# Revit family: VIESSMANN - Vitocell 100-V (CVW.CVWA) 300 L
name_source: partatom
category: Wyposażenie mechaniczne
revit_build: Autodesk Revit 2017 (Build: 20160720_1515(x64)
units: mm (PartAtom-declared; Revit-internal decimal feet)

## family parameters
Numer OmniClass = 23.65.35.11.11
Oparty na płaszczyźnie roboczej = Nie
Punkt obliczania pomieszczeń = Nie
Tnij formami wycięć po wczytaniu = Tak
Typ części = Normalny
Tytuł OmniClass = Storage Water Heaters
Współdzielony = Nie
Wymiar okrągłego złącza = Użyj średnicy
Zawsze pionowo = Tak

## types (1)
- Zbiornik CVWA 300L
    Autor = https://www.archispace.pl
    Ciepła woda użytkowa = 1"
    Cyrkulacja = 3/4"
    Czas podgrzewu cwu przy podłączonej pompie ciepła o znamionowej mocy cieplnej 16kW i temp. wody na zasilaniu wodą grzewczą wynoszącej 55 lub 65°C - przy podgrzewie cwu z 10 do 45°C = 50 min
    Czas podgrzewu cwu przy podłączonej pompie ciepła o znamionowej mocy cieplnej 16kW i temp. wody na zasilaniu wodą grzewczą wynoszącej 55 lub 65°C - przy podgrzewie cwu z 10 do 55°C = 60 min
    Grzałka elektryczna = 1 1/2"
    Ilość ciepła dyżurnego = 1.65 kWh/24h
    Ilość pobierana = 15 l/min
    Klasa efektywności energetycznej = B
    Maks. ilość pobierana przy temperaturze na zasilaniu wodą grzewczą 70℃ = 35
    Maks. ilość pobierana przy temperaturze na zasilaniu wodą grzewczą 80℃ = 40
    Maks. ilość pobierana przy temperaturze na zasilaniu wodą grzewczą 90℃ = 41
    Maks. możliwa do przyłączenia moc pompy ciepła przy temp. wody na zasilaniu wodą grzewczą wynoszącej 65°C, temp. cwu 55°C oraz podanym przepływie objętościowym wody grzewczej = 12000 W
    Maks. powierzchnia czynna absorbera możliwa do podłączenia do zestawu solarnych wymienników ciepła - Vitosol-F = 0.0 m²
    Maks. powierzchnia czynna absorbera możliwa do podłączenia do zestawu solarnych wymienników ciepła - Vitosol-T = 0.0 m²
    Masa całkowita z izolacją cieplną = 180.00 kg
    Model = Podgrzewacz pojemnościowy Viessmann Vitocell 100-V CVAA 950L / Hot water storage tank Viessmann Vitocell 100-V CVAA 950L
    Numer identyfikacyjny produktu = 9W173-13MC/E
    Objętość brutto = 322.0 L
    Objętość wody grzewczej = 22.0 L
    Opis = Podgrzewacz pojemnościowy
    Opis indeksowy = 9W173-13MC/E
    Opory przepływu po stronie wody grzewczej = 3600.0 Pa
    Opory przepływu po stronie wody użytkowej = 900.0 Pa
    Pobierana ilość cwu bez dogrzewu - zawartość podgrzewacza podgrzana o 45°C = 210.0 L
    Pobierana ilość cwu bez dogrzewu - zawartość podgrzewacza podgrzana o 55°C = 210.0 L
    Podział = 667 mm  [stored 2.18832 ft]
    Pojemność podgrzewacza = 300.0 L
    Powierzchnia grzewcza = 3.0 m²
    Powrót wody grzewczej = 1 1/4"
    Producent = Viessmann Sp.z.o.o.
    Przepływ objętościowy wody grzewczej (dla podanych wydajności stałych) = 3.00 m³/h
    Przepływ objętościowy wody grzewczej (przy podgrzewie cwu z 10 na 45℃) przy temperaturze na zasilaniu wodą grzewczą 50℃ = 0.62
    Przepływ objętościowy wody grzewczej (przy podgrzewie cwu z 10 na 45℃) przy temperaturze na zasilaniu wodą grzewczą 60℃ = 1.03
    Przepływ objętościowy wody grzewczej (przy podgrzewie cwu z 10 na 45℃) przy temperaturze na zasilaniu wodą grzewczą 70℃ = 1.40
    Przepływ objętościowy wody grzewczej (przy podgrzewie cwu z 10 na 45℃) przy temperaturze na zasilaniu wodą grzewczą 80℃ = 1.75
    Przepływ objętościowy wody grzewczej (przy podgrzewie cwu z 10 na 45℃) przy temperaturze na zasilaniu wodą grzewczą 90℃ = 2.09
    Przepływ objętościowy wody grzewczej (przy podgrzewie cwu z 10 na 60℃) przy temperaturze na zasilaniu wodą grzewczą 70℃ = 0.71
    Przepływ objętościowy wody grzewczej (przy podgrzewie cwu z 10 na 60℃) przy temperaturze na zasilaniu wodą grzewczą 80℃ = 1.00
    Przepływ objętościowy wody grzewczej (przy podgrzewie cwu z 10 na 60℃) przy temperaturze na zasilaniu wodą grzewczą 90℃ = 1.26
    Przepływ po stronie wody grzewczej = 3.00 m³/h
    Przepływ po stronie wody użytkowej = 2.09 m³/h
    Szerokość - bez izolacji cieplnej = 0 mm  [stored 0 ft]
    Szerokość - z izolacją cieplną = 744 mm
    Szerokość z izolacją cieplną = 744 mm
    URL = https://www.viessmann-projektant.pl
    Viessmann Kolor 1 = Viessmann Kolor 1
    Viessmann Kolor 2 = Viessmann Kolor 2
    Viessmann Kolor 3 = Viessmann Kolor 3
    Wsp. mocy NL w połączeniu z pompą ciepła - temp. na ładowaniu podgrzewacza cwu 45℃ = 1.7
    Wsp. mocy NL w połączeniu z pompą ciepła - temp. na ładowaniu podgrzewacza cwu 50℃ = 1.9
    Współczynnik mocy NL przy temperaturze na zasilaniu wodą grzewczą 70℃ = 7.5
    Współczynnik mocy NL przy temperaturze na zasilaniu wodą grzewczą 80℃ = 8.5
    Współczynnik mocy NL przy temperaturze na zasilaniu wodą grzewczą 90℃ = 9.5
    Wydajność krótkotrwała przy temperaturze na zasilaniu wodą grzewczą 70℃ = 357 L/10min
    Wydajność krótkotrwała przy temperaturze na zasilaniu wodą grzewczą 80℃ = 400 L/10min
    Wydajność krótkotrwała przy temperaturze na zasilaniu wodą grzewczą 90℃ = 415 L/10min
    Wydajność stała (przy podgrzewie cwu z 10 na 45℃ i temperaturze na zasilaniu wodą grzewczą 50℃ = 25000
    Wydajność stała (przy podgrzewie cwu z 10 na 45℃ i temperaturze na zasilaniu wodą grzewczą 60℃ = 42000
    Wydajność stała (przy podgrzewie cwu z 10 na 45℃ i temperaturze na zasilaniu wodą grzewczą 70℃ = 57000
    Wydajność stała (przy podgrzewie cwu z 10 na 45℃ i temperaturze na zasilaniu wodą grzewczą 80℃ = 71000
    Wydajność stała (przy podgrzewie cwu z 10 na 45℃ i temperaturze na zasilaniu wodą grzewczą 90℃ = 85000
    Wydajność stała (przy podgrzewie cwu z 10 na 60℃ i temperaturze na zasilaniu wodą grzewczą 70℃ = 41000
    Wydajność stała (przy podgrzewie cwu z 10 na 60℃ i temperaturze na zasilaniu wodą grzewczą 80℃ = 58000
    Wydajność stała (przy podgrzewie cwu z 10 na 60℃ i temperaturze na zasilaniu wodą grzewczą 90℃ = 73000
    Wymiar przechylenia - bez izolacji cieplnej = 0 mm  [stored 0 ft]
    Wymiar przechylenia - z izolacją cieplną = 1825 mm
    Wysokośc z izolacją = 1734 mm  [stored 5.68898 ft]
    Wysokość - bez izolacji cieplnej = 0 mm  [stored 0 ft]
    Wysokość - z izolacją cieplną = 1734 mm  [stored 5.68898 ft]
    Wysokość króćca cwu = 1601 mm
    Wysokość króćca cyrkulacji = 1137 mm
    Wysokość króćca powrotu wody grzewczej = 261 mm
    Wysokość króćca zasilania wodą grzewczą = 967 mm
    Wysokość króćca zwu = 77 mm
    Zasilanie wody grzewczej = 1 1/4"
    Zestaw solarnych wymienników ciepła = 0"
    Zimna woda użytkowa = 1"
    Średnica - bez izolacji cieplnej = 0 mm  [stored 0 ft]
    Średnica - z izolacją cieplną = 667 mm  [stored 2.18832 ft]
    Średnica z izolacją cieplną = 667 mm  [stored 2.18832 ft]

note: source unit labels omitted for Maks. ilość pobierana przy temperaturze na zasilaniu wodą grzewczą 70℃, Maks. ilość pobierana przy temperaturze na zasilaniu wodą grzewczą 80℃, Maks. ilość pobierana przy temperaturze na zasilaniu wodą grzewczą 90℃, Przepływ objętościowy wody grzewczej (przy podgrzewie cwu z 10 na 45℃) przy temperaturze na zasilaniu wodą grzewczą 50℃, Przepływ objętościowy wody grzewczej (przy podgrzewie cwu z 10 na 45℃) przy temperaturze na zasilaniu wodą grzewczą 60℃, Przepływ objętościowy wody grzewczej (przy podgrzewie cwu z 10 na 45℃) przy temperaturze na zasilaniu wodą grzewczą 70℃, Przepływ objętościowy wody grzewczej (przy podgrzewie cwu z 10 na 45℃) przy temperaturze na zasilaniu wodą grzewczą 80℃, Przepływ objętościowy wody grzewczej (przy podgrzewie cwu z 10 na 45℃) przy temperaturze na zasilaniu wodą grzewczą 90℃, Przepływ objętościowy wody grzewczej (przy podgrzewie cwu z 10 na 60℃) przy temperaturze na zasilaniu wodą grzewczą 70℃, Przepływ objętościowy wody grzewczej (przy podgrzewie cwu z 10 na 60℃) przy temperaturze na zasilaniu wodą grzewczą 80℃, Przepływ objętościowy wody grzewczej (przy podgrzewie cwu z 10 na 60℃) przy temperaturze na zasilaniu wodą grzewczą 90℃, Wydajność stała (przy podgrzewie cwu z 10 na 45℃ i temperaturze na zasilaniu wodą grzewczą 50℃, Wydajność stała (przy podgrzewie cwu z 10 na 45℃ i temperaturze na zasilaniu wodą grzewczą 60℃, Wydajność stała (przy podgrzewie cwu z 10 na 45℃ i temperaturze na zasilaniu wodą grzewczą 70℃, Wydajność stała (przy podgrzewie cwu z 10 na 45℃ i temperaturze na zasilaniu wodą grzewczą 80℃, Wydajność stała (przy podgrzewie cwu z 10 na 45℃ i temperaturze na zasilaniu wodą grzewczą 90℃, Wydajność stała (przy podgrzewie cwu z 10 na 60℃ i temperaturze na zasilaniu wodą grzewczą 70℃, Wydajność stała (przy podgrzewie cwu z 10 na 60℃ i temperaturze na zasilaniu wodą grzewczą 80℃, Wydajność stała (przy podgrzewie cwu z 10 na 60℃ i temperaturze na zasilaniu wodą grzewczą 90℃ — the stored unit's dimension contradicts the parameter name (converter mislabeling)

note: [stored X ft] marks values corroborated as IEEE doubles in the binary element streams (Revit-internal decimal feet)
